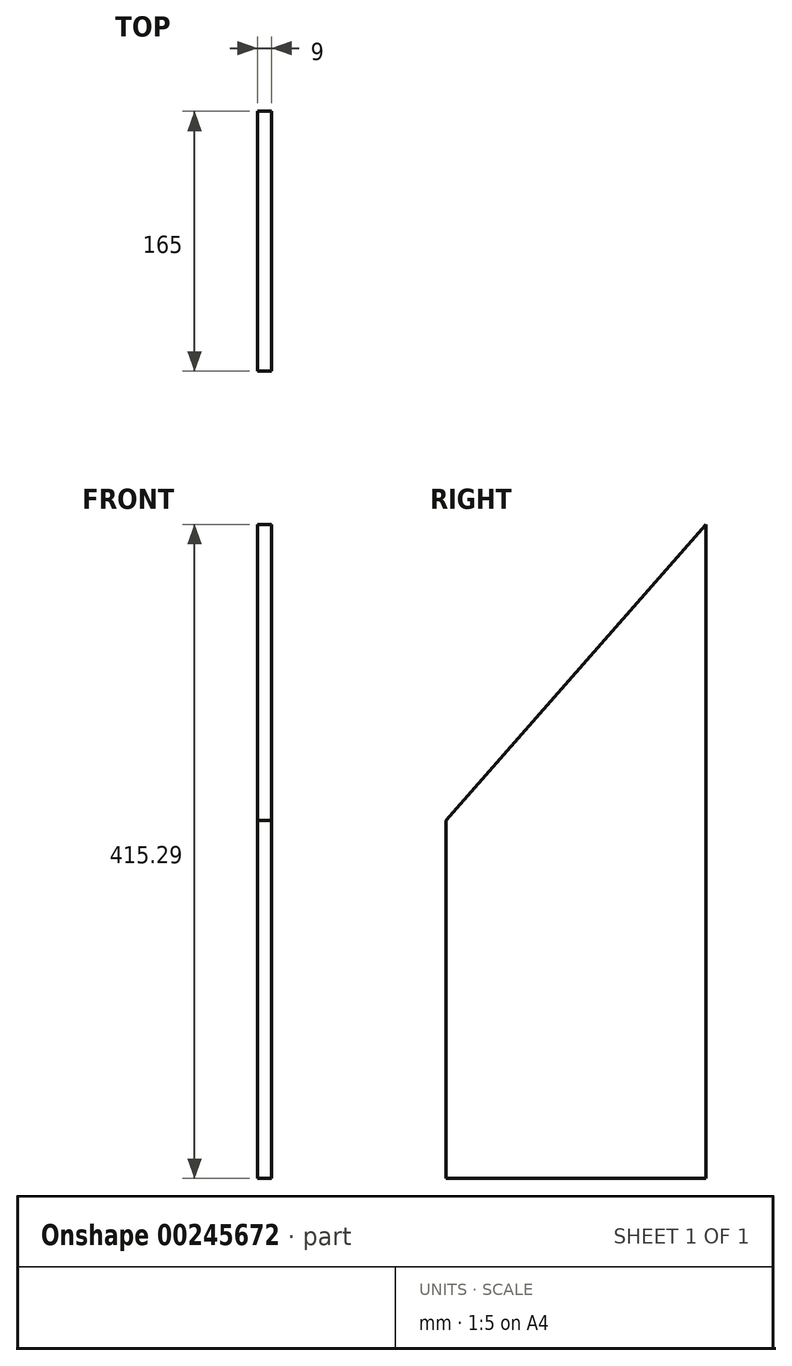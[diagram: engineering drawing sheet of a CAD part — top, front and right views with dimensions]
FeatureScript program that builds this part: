
annotation { "Feature Type Name" : "Feature", "Feature Type Description" : "" }
export const myFeature = defineFeature(function(context is Context, id is Id, definition is map)
    precondition{}
    {
        {
            var Q0;
            Q0=qCreatedBy(makeId("Right.planeOp"),FACE);
            var sketch = newSketch(context, id + "F0", { "sketchPlane" : qUnion([Q0])});
            skLineSegment(sketch, "E0.bottom", {"start": v(82.5, 100) * mm, "end": v(-82.5, 100) * mm});
            skLineSegment(sketch, "E0.top", {"start": v(82.5, -100) * mm, "end": v(-82.5, -100) * mm});
            skLineSegment(sketch, "E0.left", {"start": v(82.5, 100) * mm, "end": v(82.5, -100) * mm});
            skLineSegment(sketch, "E0.right", {"start": v(-82.5, 100) * mm, "end": v(-82.5, -100) * mm});
            skPoint(sketch, "E0.middle", {"position": v(0, 0) * mm});
            skLineSegment(sketch, "E1", {"start": v(-82.5, 100) * mm, "end": v(82.5, 288) * mm});
            skLineSegment(sketch, "E2", {"start": v(82.5, 288) * mm, "end": v(82.5, 100) * mm});
            skLineSegment(sketch, "E3.0", {"start": v(-96.03, 111.87) * mm, "end": v(68.97, 299.87) * mm, "construction": true});
            skLineSegment(sketch, "E4", {"start": v(-82.5, 100) * mm, "end": v(-82.5, 127.29) * mm});
            skLineSegment(sketch, "E5", {"start": v(-82.5, 127.29) * mm, "end": v(82.5, 315.29) * mm});
            skLineSegment(sketch, "E6", {"start": v(82.5, 315.29) * mm, "end": v(82.5, 288) * mm});
            skSolve(sketch);
        }
        {
            var Q0;
            Q0 = qSketchRegion(id + "F0", true);
            extrude(context, id + "F1", {"entities" : qUnion([Q0]), "depth" : 9 * mm});
        }
    });
